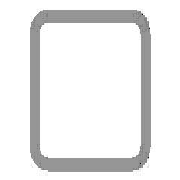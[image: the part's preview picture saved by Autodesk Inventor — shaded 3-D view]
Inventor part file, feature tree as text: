
AUTODESK INVENTOR PART (.ipt)
format: ipt  version: 2025 (Build 290162010, 162A)  size: 134,656 bytes
history: native  units: mm (DEFAULTED — no unit token found)
features: other x4, sketch x1, plane x1
ambient origin geometry x8: Origin, YZ Plane, XZ Plane, XY Plane, X Axis, Y Axis, Z Axis, Center Point
bodies: Solid1 (feature_tree), Body (feature_tree)
feature tree (6):
  parser-record x1  (decoder bookkeeping rows leaked as tree rows — omitted from the tree; the rows remain in map.json)
  other  "Driven Length"
  other  "Start Plane"
  other  "End Plane"
  sketch  "Sketch3"  dims[d3=710.0mm d4=0.0mm d7=4.0mm d9=40.0mm d11=40.0mm d12=2.0mm d13=20.0mm d14=730.0mm d15=20.0mm d16=20.0mm d17=90.0deg d18=710.0mm]
  plane  "Work Plane3"
